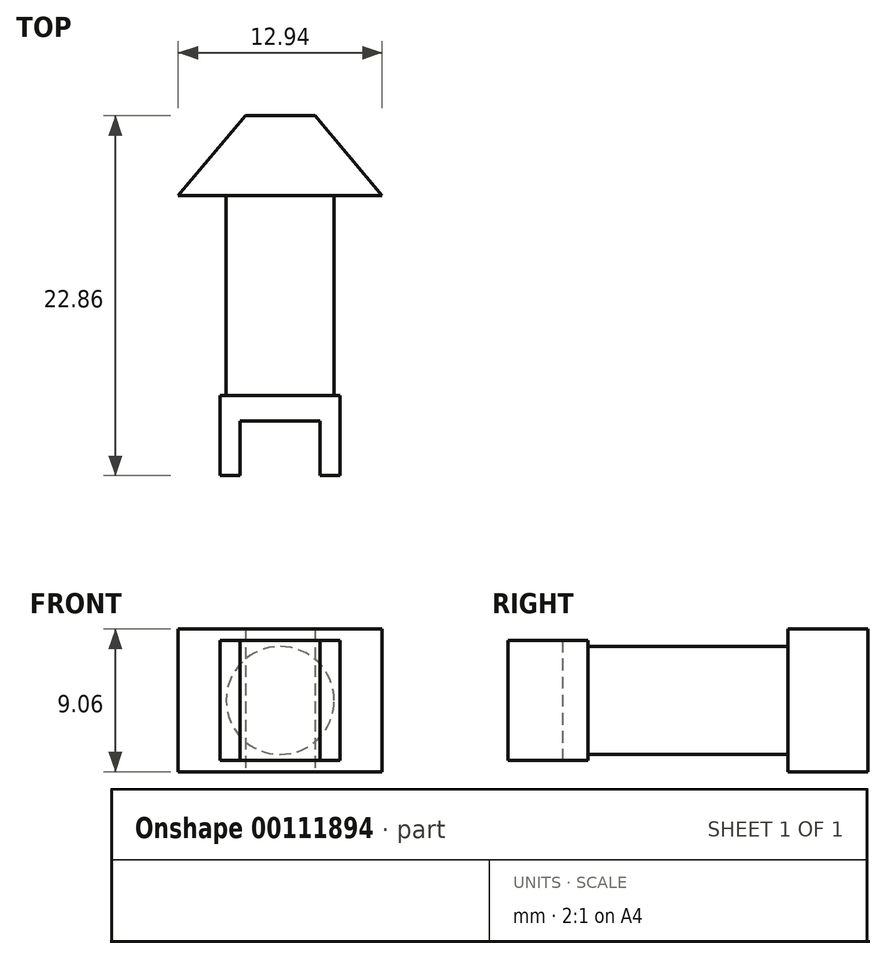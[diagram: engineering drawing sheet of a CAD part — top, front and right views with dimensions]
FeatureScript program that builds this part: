
annotation { "Feature Type Name" : "Feature", "Feature Type Description" : "" }
export const myFeature = defineFeature(function(context is Context, id is Id, definition is map)
    precondition{}
    {
        {
            var Q0;
            Q0=qCreatedBy(makeId("Front.planeOp"),FACE);
            var sketch = newSketch(context, id + "F0", { "sketchPlane" : qUnion([Q0])});
            skLineSegment(sketch, "E0.bottom", {"start": v(3.81, 3.81) * mm, "end": v(-3.8, 3.81) * mm});
            skLineSegment(sketch, "E0.top", {"start": v(3.81, -3.81) * mm, "end": v(-3.81, -3.81) * mm});
            skLineSegment(sketch, "E0.left", {"start": v(3.81, 3.81) * mm, "end": v(3.81, -3.81) * mm});
            skLineSegment(sketch, "E0.right", {"start": v(-3.8, 3.81) * mm, "end": v(-3.81, -3.81) * mm});
            skPoint(sketch, "E0.middle", {"position": v(0, 0) * mm});
            skSolve(sketch);
        }
        {
            var Q0;
            Q0 = qSketchRegion(id + "F0", true);
            extrude(context, id + "F1", {"entities" : qUnion([Q0]), "depth" : 5.08 * mm});
        }
        {
            var Q0;
            Q0=makeQuery(id+"F1.opExtrude","SWEPT_FACE",FACE,{"disambiguationData":[OSD([sQuery(id+"F0.wireOp",EDGE,"E0.top")])]});
            var sketch = newSketch(context, id + "F2", { "sketchPlane" : qUnion([Q0])});
            skLineSegment(sketch, "E1.bottom", {"start": v(0, 1.62) * mm, "end": v(-2.54, 1.62) * mm});
            skLineSegment(sketch, "E1.top", {"start": v(0, 5.08) * mm, "end": v(-2.54, 5.08) * mm});
            skLineSegment(sketch, "E1.right", {"start": v(-2.54, 1.62) * mm, "end": v(-2.54, 5.08) * mm});
            skLineSegment(sketch, "E2.MirrorCS", {"start": v(2.54, 1.62) * mm, "end": v(2.54, 5.08) * mm});
            skLineSegment(sketch, "E3.MirrorCS", {"start": v(0, 1.62) * mm, "end": v(2.54, 1.62) * mm});
            skSolve(sketch);
        }
        {
            var Q0;
            Q0 = qSketchRegion(id + "F2", true);
            var Q1;
            Q1=makeQuery(id+"F2.imprint","IMPRINT",FACE,{"disambiguationData":[TD([[makeQuery(id+"F2.imprint","IMPRINT",EDGE,{"derivedFrom":sQuery(id+"F2.wireOp",EDGE,"E1.bottom")}),-1.0]])]});
            extrude(context, id + "F3", {"entities" : qUnion([Q0, Q1]), "operationType" : NewBodyOperationType.REMOVE, "oppositeDirection" : true, "depth" : 25.4 * mm});
        }
        {
            var Q0;
            Q0=makeQuery(id+"F1.opExtrude","CAP_FACE",FACE,{"disambiguationData":[OSD([sQuery(id+"F0.wireOp",EDGE,"E0.bottom"),sQuery(id+"F0.wireOp",EDGE,"E0.top"),sQuery(id+"F0.wireOp",EDGE,"E0.left"),sQuery(id+"F0.wireOp",EDGE,"E0.right")])],"isStart":true});
            var sketch = newSketch(context, id + "F4", { "sketchPlane" : qUnion([Q0])});
            skCircle(sketch, "E4", {"center": v(0, 0) * mm, "radius": 3.43 * mm});
            skSolve(sketch);
        }
        {
            var Q0;
            Q0 = qSketchRegion(id + "F4", true);
            extrude(context, id + "F5", {"entities" : qUnion([Q0]), "depth" : 12.7 * mm});
        }
        {
            var Q0;
            Q0=makeQuery(id+"F5.opExtrude","CAP_FACE",FACE,{"disambiguationData":[OSD([sQuery(id+"F4.wireOp",EDGE,"E4")])],"isStart":false});
            var sketch = newSketch(context, id + "F6", { "sketchPlane" : qUnion([Q0])});
            skLineSegment(sketch, "E5.bottom", {"start": v(-6.47, 4.53) * mm, "end": v(6.47, 4.53) * mm});
            skLineSegment(sketch, "E5.top", {"start": v(-6.47, -4.53) * mm, "end": v(6.47, -4.53) * mm});
            skLineSegment(sketch, "E5.left", {"start": v(-6.47, 4.53) * mm, "end": v(-6.47, -4.53) * mm});
            skLineSegment(sketch, "E5.right", {"start": v(6.47, 4.53) * mm, "end": v(6.47, -4.53) * mm});
            skPoint(sketch, "E5.middle", {"position": v(0, 0) * mm});
            skSolve(sketch);
        }
        {
            var Q0;
            Q0 = qSketchRegion(id + "F6", true);
            extrude(context, id + "F7", {"entities" : qUnion([Q0]), "operationType" : NewBodyOperationType.ADD, "depth" : 5.08 * mm});
        }
        {
            var Q0;
            Q0=makeQuery(id+"F7.opExtrude","SWEPT_FACE",FACE,{"disambiguationData":[OSD([sQuery(id+"F6.wireOp",EDGE,"E5.top")])]});
            var sketch = newSketch(context, id + "F8", { "sketchPlane" : qUnion([Q0])});
            skLineSegment(sketch, "E6", {"start": v(-6.47, -12.7) * mm, "end": v(-2.2, -17.78) * mm});
            skLineSegment(sketch, "E7", {"start": v(-2.2, -17.78) * mm, "end": v(2.2, -17.78) * mm});
            skLineSegment(sketch, "E8.MirrorCS", {"start": v(6.47, -12.7) * mm, "end": v(2.2, -17.78) * mm});
            skSolve(sketch);
        }
        {
            var Q0;
            Q0 = qSketchRegion(id + "F8", true);
            var Q1;
            {var subQ0=sQuery(id+"F8.wireOp",EDGE,"E6");Q1=makeQuery(id+"F8.imprint","IMPRINT",FACE,{"disambiguationData":[TD([[makeQuery(id+"F8.imprint","IMPRINT",EDGE,{"derivedFrom":subQ0}),-1.0]])]});}
            var Q2;
            {var subQ0=sQuery(id+"F8.wireOp",EDGE,"E8.MirrorCS");Q2=makeQuery(id+"F8.imprint","IMPRINT",FACE,{"disambiguationData":[TD([[makeQuery(id+"F8.imprint","IMPRINT",EDGE,{"derivedFrom":subQ0}),1.0]])]});}
            extrude(context, id + "F9", {"entities" : qUnion([Q0, Q1, Q2]), "operationType" : NewBodyOperationType.REMOVE, "oppositeDirection" : true, "depth" : 25.4 * mm});
        }
    });
